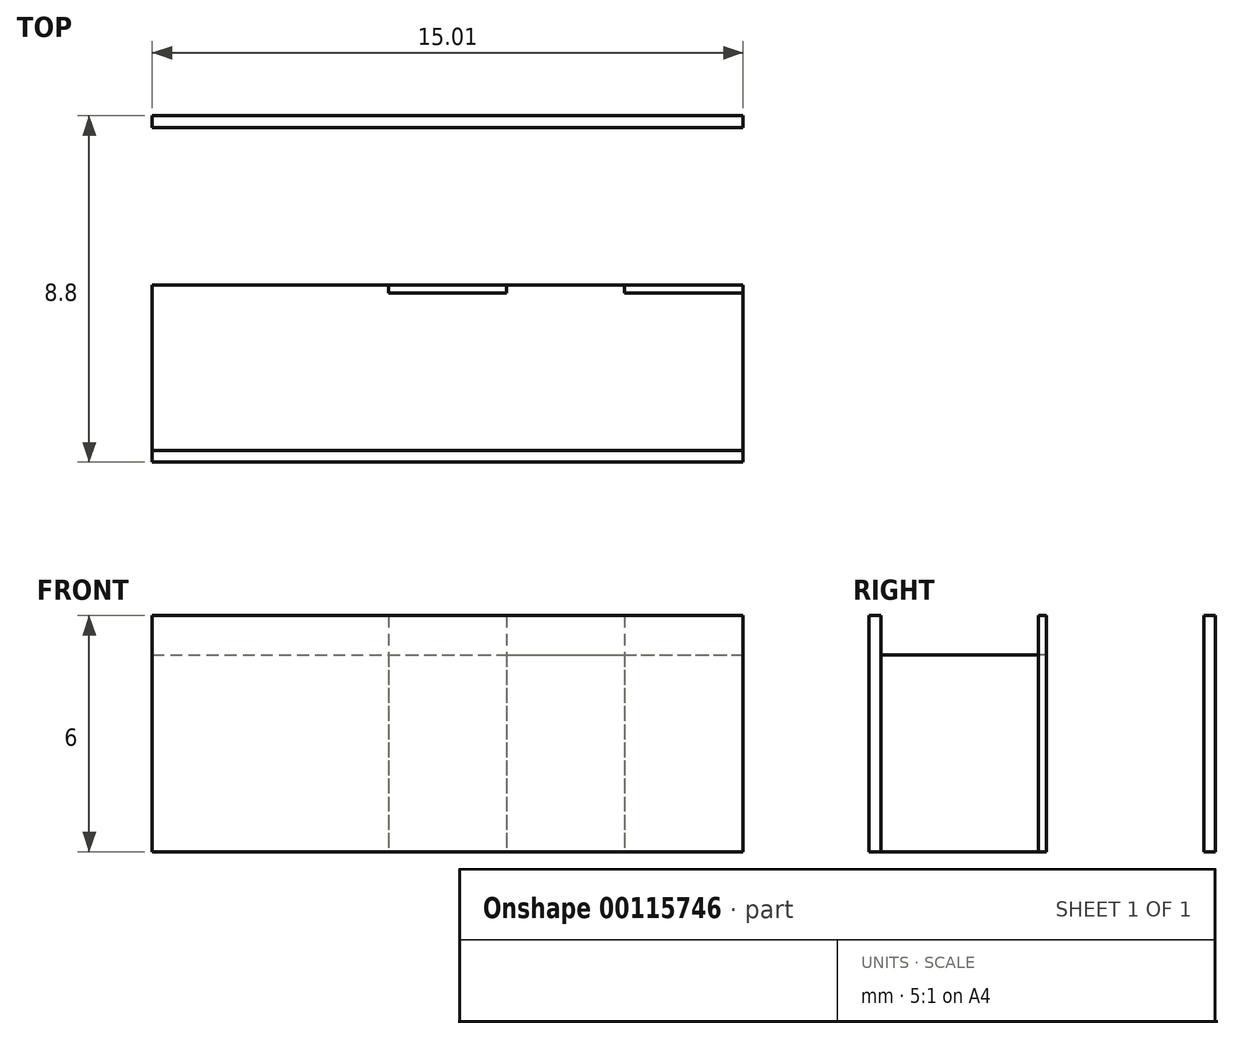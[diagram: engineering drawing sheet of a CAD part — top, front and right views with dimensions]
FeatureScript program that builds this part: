
annotation { "Feature Type Name" : "Feature", "Feature Type Description" : "" }
export const myFeature = defineFeature(function(context is Context, id is Id, definition is map)
    precondition{}
    {
        {
            var Q0;
            Q0=qCreatedBy(makeId("Top.planeOp"),FACE);
            var sketch = newSketch(context, id + "F0", { "sketchPlane" : qUnion([Q0])});
            skLineSegment(sketch, "E0.bottom", {"start": v(0, 4) * mm, "end": v(15, 4) * mm});
            skLineSegment(sketch, "E0.top", {"start": v(0, 0) * mm, "end": v(15, 0) * mm});
            skLineSegment(sketch, "E0.left", {"start": v(0, 4) * mm, "end": v(0, 0) * mm});
            skLineSegment(sketch, "E0.right", {"start": v(15, 4) * mm, "end": v(15, 0) * mm});
            skLineSegment(sketch, "E1.bottom", {"start": v(0, 8.2) * mm, "end": v(15, 8.2) * mm});
            skLineSegment(sketch, "E1.left", {"start": v(0, 8.2) * mm, "end": v(0, 4) * mm});
            skLineSegment(sketch, "E1.right", {"start": v(15, 8.2) * mm, "end": v(15, 4) * mm});
            skLineSegment(sketch, "E2", {"start": v(0, 4.2) * mm, "end": v(15, 4.2) * mm});
            skLineSegment(sketch, "E3", {"start": v(0, 4.2) * mm, "end": v(0, 4) * mm});
            skLineSegment(sketch, "E4.1.0.0", {"start": v(3, 4.2) * mm, "end": v(3, 4) * mm});
            skLineSegment(sketch, "E4.2.0.0", {"start": v(6, 4.2) * mm, "end": v(6, 4) * mm});
            skLineSegment(sketch, "E4.3.0.0", {"start": v(9, 4.2) * mm, "end": v(9, 4) * mm});
            skLineSegment(sketch, "E4.4.0.0", {"start": v(12, 4.2) * mm, "end": v(12, 4) * mm});
            skLineSegment(sketch, "E4.5.0.0", {"start": v(15, 4.2) * mm, "end": v(15, 4) * mm});
            skLineSegment(sketch, "E4.direction1", {"start": v(0, 4) * mm, "end": v(3, 4) * mm, "construction": true});
            skLineSegment(sketch, "E5.top", {"start": v(0, 8.5) * mm, "end": v(15, 8.5) * mm});
            skLineSegment(sketch, "E5.left", {"start": v(0, 8.2) * mm, "end": v(0, 8.5) * mm});
            skLineSegment(sketch, "E5.right", {"start": v(15, 8.2) * mm, "end": v(15, 8.5) * mm});
            skLineSegment(sketch, "E6.top", {"start": v(0, -0.3) * mm, "end": v(15, -0.3) * mm});
            skLineSegment(sketch, "E6.left", {"start": v(0, 0) * mm, "end": v(0, -0.3) * mm});
            skLineSegment(sketch, "E6.right", {"start": v(15, 0) * mm, "end": v(15, -0.3) * mm});
            skSolve(sketch);
        }
        {
            var Q0;
            {var subQ3=sQuery(id+"F0.wireOp",EDGE,"E1.left");Q0=makeQuery(id+"F0.imprint","IMPRINT",FACE,{"disambiguationData":[TD([[makeQuery(id+"F0.imprint","IMPRINT",EDGE,{"derivedFrom":subQ3}),1.0]])]});}
            var Q1;
            {var subQ0=sQuery(id+"F0.wireOp",EDGE,"E4.1.0.0");Q1=makeQuery(id+"F0.imprint","IMPRINT",FACE,{"disambiguationData":[TD([[makeQuery(id+"F0.imprint","IMPRINT",EDGE,{"derivedFrom":subQ0}),1.0]])]});}
            var Q2;
            {var subQ3=sQuery(id+"F0.wireOp",EDGE,"E0.left");Q2=makeQuery(id+"F0.imprint","IMPRINT",FACE,{"disambiguationData":[TD([[makeQuery(id+"F0.imprint","IMPRINT",EDGE,{"derivedFrom":subQ3}),1.0]])]});}
            var Q3;
            {var subQ0=sQuery(id+"F0.wireOp",EDGE,"E4.3.0.0");Q3=makeQuery(id+"F0.imprint","IMPRINT",FACE,{"disambiguationData":[TD([[makeQuery(id+"F0.imprint","IMPRINT",EDGE,{"derivedFrom":subQ0}),1.0]])]});}
            extrude(context, id + "F1", {"entities" : qUnion([Q0, Q1, Q2, Q3]), "depth" : 5 * mm});
        }
        {
            var Q0;
            Q0=makeQuery(id+"F0.imprint","IMPRINT",FACE,{"disambiguationData":[TD([[makeQuery(id+"F0.imprint","IMPRINT",EDGE,{"derivedFrom":sQuery(id+"F0.wireOp",EDGE,"E5.top")}),-1.0]])]});
            var Q1;
            {var subQ0=sQuery(id+"F0.wireOp",EDGE,"E3");Q1=makeQuery(id+"F0.imprint","IMPRINT",FACE,{"disambiguationData":[TD([[makeQuery(id+"F0.imprint","IMPRINT",EDGE,{"derivedFrom":subQ0}),1.0]])]});}
            var Q2;
            {var subQ0=sQuery(id+"F0.wireOp",EDGE,"E4.2.0.0");Q2=makeQuery(id+"F0.imprint","IMPRINT",FACE,{"disambiguationData":[TD([[makeQuery(id+"F0.imprint","IMPRINT",EDGE,{"derivedFrom":subQ0}),1.0]])]});}
            var Q3;
            {var subQ2=sQuery(id+"F0.wireOp",EDGE,"E4.4.0.0");Q3=makeQuery(id+"F0.imprint","IMPRINT",FACE,{"disambiguationData":[TD([[makeQuery(id+"F0.imprint","IMPRINT",EDGE,{"derivedFrom":subQ2}),1.0]])]});}
            var Q4;
            Q4=makeQuery(id+"F0.imprint","IMPRINT",FACE,{"disambiguationData":[TD([[makeQuery(id+"F0.imprint","IMPRINT",EDGE,{"derivedFrom":sQuery(id+"F0.wireOp",EDGE,"E0.top")}),-1.0]])]});
            extrude(context, id + "F2", {"entities" : qUnion([Q0, Q1, Q2, Q3, Q4]), "depth" : 6 * mm});
        }
    });
